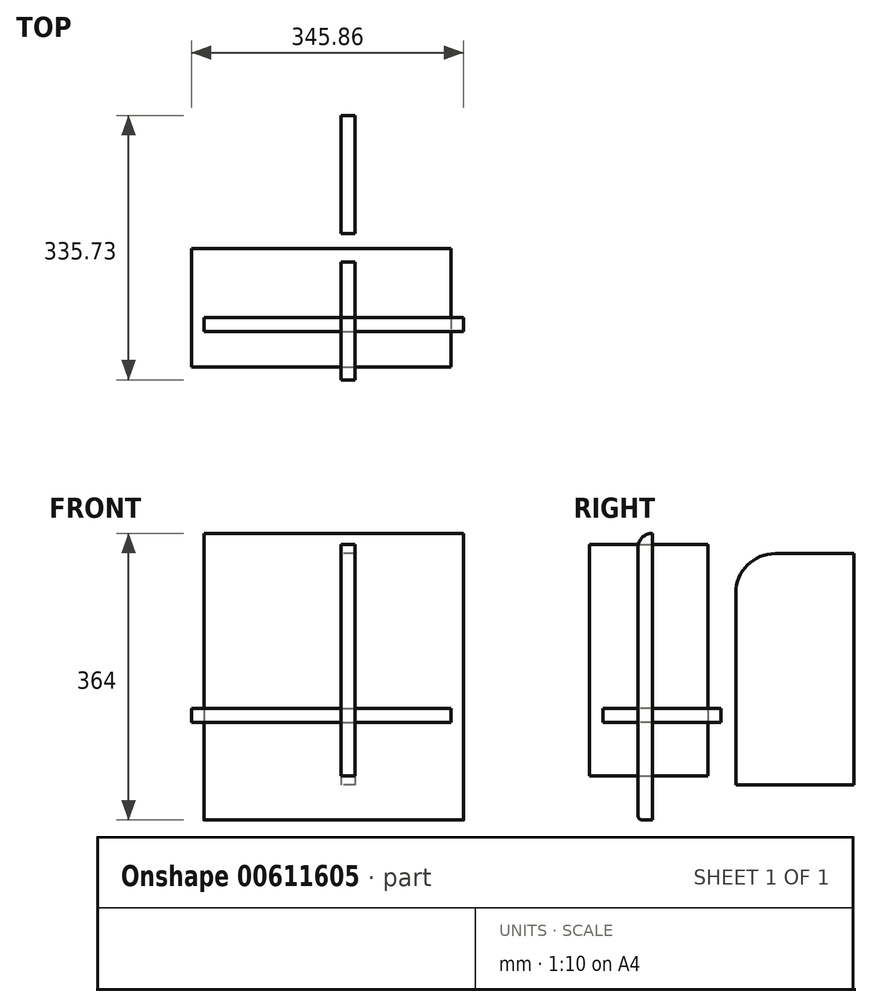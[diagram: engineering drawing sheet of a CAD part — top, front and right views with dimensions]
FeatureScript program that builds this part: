
annotation { "Feature Type Name" : "Feature", "Feature Type Description" : "" }
export const myFeature = defineFeature(function(context is Context, id is Id, definition is map)
    precondition{}
    {
        {
            var Q0;
            Q0=qCreatedBy(makeId("Top.planeOp"),FACE);
            var sketch = newSketch(context, id + "F0", { "sketchPlane" : qUnion([Q0])});
            skLineSegment(sketch, "E0.bottom", {"start": v(-189.98, 87.17) * mm, "end": v(140.02, 87.17) * mm});
            skLineSegment(sketch, "E0.top", {"start": v(-189.98, -62.83) * mm, "end": v(140.02, -62.83) * mm});
            skLineSegment(sketch, "E0.left", {"start": v(-189.98, 87.17) * mm, "end": v(-189.98, -62.83) * mm});
            skLineSegment(sketch, "E0.right", {"start": v(140.02, 87.17) * mm, "end": v(140.02, -62.83) * mm});
            skSolve(sketch);
        }
        {
            var Q0;
            Q0=makeQuery(id+"F0.imprint","IMPRINT",FACE,{"disambiguationData":[TD([[makeQuery(id+"F0.imprint","IMPRINT",EDGE,{"derivedFrom":sQuery(id+"F0.wireOp",EDGE,"E0.bottom")}),-1.0]])]});
            extrude(context, id + "F1", {"entities" : qUnion([Q0]), "depth" : 18 * mm, "offsetDistance" : 25 * mm});
        }
        {
            var Q0;
            Q0=qCreatedBy(makeId("Right.planeOp"),FACE);
            var sketch = newSketch(context, id + "F2", { "sketchPlane" : qUnion([Q0])});
            skLineSegment(sketch, "E1.bottom", {"start": v(-79.42, 226.32) * mm, "end": v(70.58, 226.32) * mm});
            skLineSegment(sketch, "E1.top", {"start": v(-79.42, -67.68) * mm, "end": v(70.58, -67.68) * mm});
            skLineSegment(sketch, "E1.left", {"start": v(-79.42, 226.32) * mm, "end": v(-79.42, -67.68) * mm});
            skLineSegment(sketch, "E1.right", {"start": v(70.58, 226.32) * mm, "end": v(70.58, -67.68) * mm});
            skSolve(sketch);
        }
        {
            var Q0;
            Q0=makeQuery(id+"F2.imprint","IMPRINT",FACE,{"disambiguationData":[TD([[makeQuery(id+"F2.imprint","IMPRINT",EDGE,{"derivedFrom":sQuery(id+"F2.wireOp",EDGE,"E1.bottom")}),-1.0]])]});
            extrude(context, id + "F3", {"entities" : qUnion([Q0]), "depth" : 18 * mm, "offsetDistance" : 25 * mm});
        }
        {
            var Q0;
            Q0=qCreatedBy(makeId("Right.planeOp"),FACE);
            var sketch = newSketch(context, id + "F4", { "sketchPlane" : qUnion([Q0])});
            skLineSegment(sketch, "E2.top", {"start": v(106.31, -79.28) * mm, "end": v(256.31, -79.28) * mm});
            skLineSegment(sketch, "E2.left", {"start": v(106.31, 164.77) * mm, "end": v(106.31, 164.72) * mm});
            skLineSegment(sketch, "E2.right", {"start": v(256.31, 214.72) * mm, "end": v(256.31, -79.28) * mm});
            skLineSegment(sketch, "E3", {"start": v(156.31, 214.72) * mm, "end": v(156.31, 164.72) * mm, "construction": true});
            skLineSegment(sketch, "E4", {"start": v(156.31, 164.72) * mm, "end": v(106.31, 164.72) * mm, "construction": true});
            skLineSegment(sketch, "E5", {"start": v(156.3, 214.72) * mm, "end": v(256.31, 214.72) * mm});
            skLineSegment(sketch, "E6", {"start": v(106.31, 164.77) * mm, "end": v(106.31, -79.28) * mm});
            skLineSegment(sketch, "E7", {"start": v(106.31, 164.72) * mm, "end": v(106.31, 164.72) * mm});
            skArc(sketch, "E8", {"start": v(156.31, 214.72) * mm, "mid": v(120.96, 200.08) * mm, "end": v(106.31, 164.72) * mm});
            skSolve(sketch);
        }
        {
            var Q0;
            Q0=makeQuery(id+"F4.imprint","IMPRINT",FACE,{"disambiguationData":[TD([[makeQuery(id+"F4.imprint","IMPRINT",EDGE,{"derivedFrom":sQuery(id+"F4.wireOp",EDGE,"E2.top")}),1.0]])]});
            var sketch = newSketch(context, id + "F5", { "sketchPlane" : qUnion([Q0])});
            skSolve(sketch);
        }
        {
            var Q0;
            Q0=makeQuery(id+"F5.imprint","IMPRINT",FACE,{"disambiguationData":[TD([[makeQuery(id+"F5.imprint","IMPRINT",EDGE,{"derivedFrom":makeQuery(id+"F4.imprint","IMPRINT",EDGE,{"derivedFrom":sQuery(id+"F4.wireOp",EDGE,"E2.top")})}),1.0]])]});
            extrude(context, id + "F6", {"entities" : qUnion([Q0]), "depth" : 18 * mm, "offsetDistance" : 25 * mm});
        }
        {
            var Q0;
            Q0=qCreatedBy(makeId("Front.planeOp"),FACE);
            var sketch = newSketch(context, id + "F7", { "sketchPlane" : qUnion([Q0])});
            skLineSegment(sketch, "E9.bottom", {"start": v(-174.12, 240.37) * mm, "end": v(155.88, 240.37) * mm});
            skLineSegment(sketch, "E9.top", {"start": v(-174.12, -123.63) * mm, "end": v(155.88, -123.63) * mm});
            skLineSegment(sketch, "E9.left", {"start": v(-174.12, 240.37) * mm, "end": v(-174.12, -123.63) * mm});
            skLineSegment(sketch, "E9.right", {"start": v(155.88, 240.37) * mm, "end": v(155.88, -123.63) * mm});
            skSolve(sketch);
        }
        {
            var Q0;
            Q0=makeQuery(id+"F7.imprint","IMPRINT",FACE,{"disambiguationData":[TD([[makeQuery(id+"F7.imprint","IMPRINT",EDGE,{"derivedFrom":sQuery(id+"F7.wireOp",EDGE,"E9.bottom")}),-1.0]])]});
            extrude(context, id + "F8", {"entities" : qUnion([Q0]), "depth" : 18 * mm, "offsetDistance" : 25 * mm});
        }
        {
            var Q0;
            Q0=makeQuery(id+"F8.opExtrude","CAP_EDGE",EDGE,{"disambiguationData":[OSD([sQuery(id+"F7.wireOp",EDGE,"E9.top")])],"isStart":false});
            fillet(context, id + "F9", {"entities" : qUnion([Q0]), "radius" : 5 * mm, "tangentPropagation" : true, "allowEdgeOverflow" : false});
        }
        {
            var Q0;
            Q0=makeQuery(id+"F8.opExtrude","CAP_EDGE",EDGE,{"disambiguationData":[OSD([sQuery(id+"F7.wireOp",EDGE,"E9.bottom")])],"isStart":false});
            fillet(context, id + "F10", {"entities" : qUnion([Q0]), "radius" : 18 * mm, "tangentPropagation" : true, "allowEdgeOverflow" : false});
        }
    });
